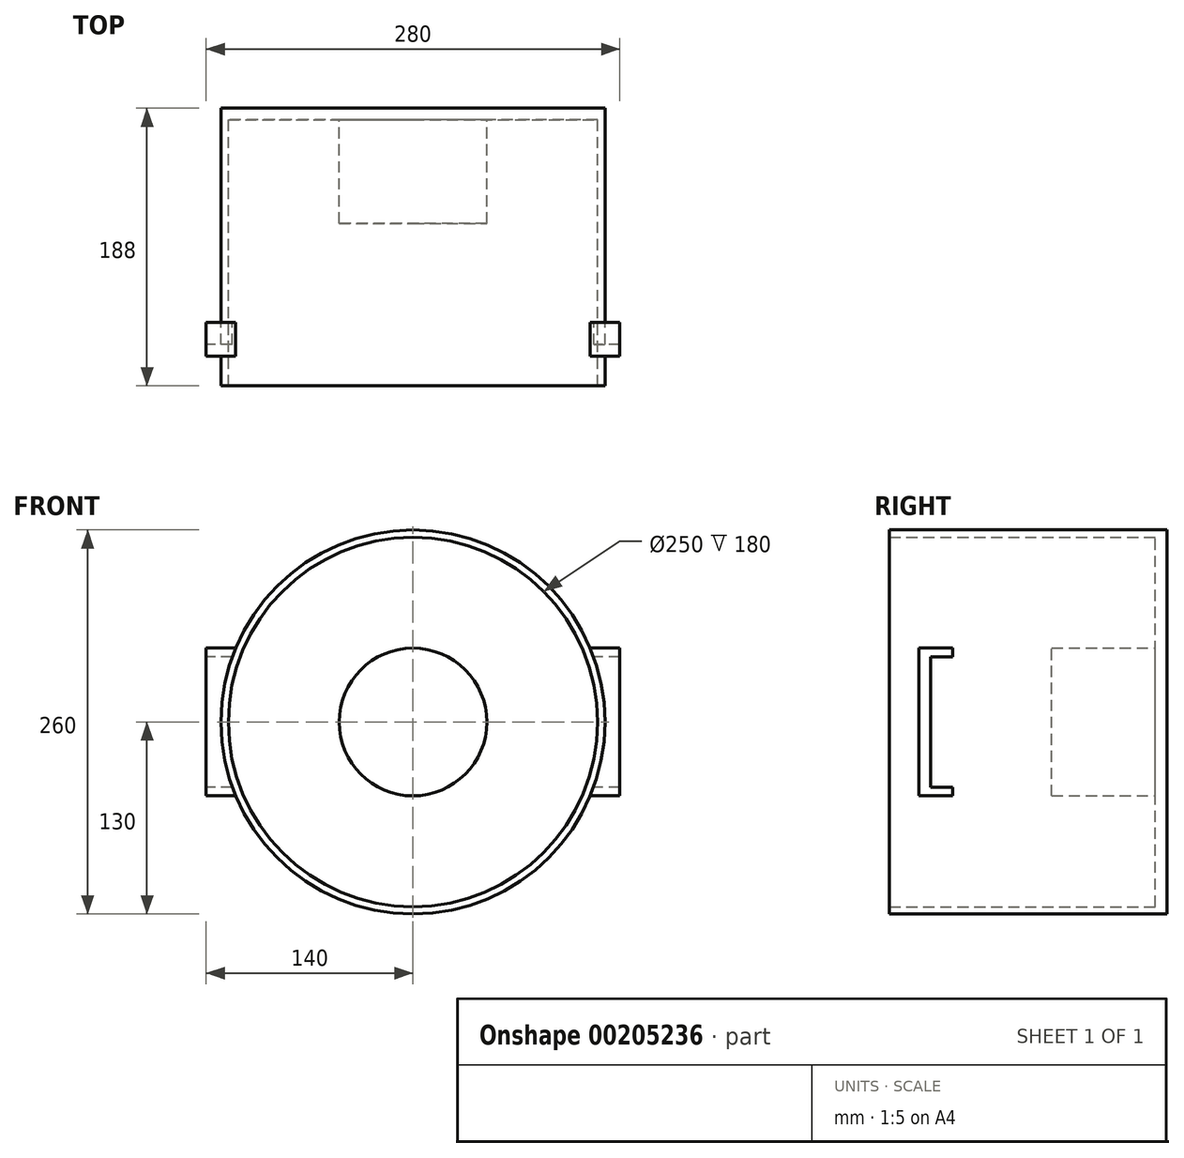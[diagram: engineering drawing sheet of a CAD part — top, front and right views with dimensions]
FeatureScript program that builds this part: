
annotation { "Feature Type Name" : "Feature", "Feature Type Description" : "" }
export const myFeature = defineFeature(function(context is Context, id is Id, definition is map)
    precondition{}
    {
        {
            var Q0;
            Q0=qCreatedBy(makeId("Front.planeOp"),FACE);
            var sketch = newSketch(context, id + "F0", { "sketchPlane" : qUnion([Q0])});
            skCircle(sketch, "E0", {"center": v(0, 0) * mm, "radius": 130 * mm});
            skSolve(sketch);
        }
        {
            var Q0;
            Q0 = qSketchRegion(id + "F0", true);
            extrude(context, id + "F1", {"entities" : qUnion([Q0]), "depth" : 8 * mm});
        }
        {
            var Q0;
            Q0=makeQuery(id+"F1.opExtrude","CAP_FACE",FACE,{"disambiguationData":[OSD([sQuery(id+"F0.wireOp",EDGE,"E0")])],"isStart":false});
            var sketch = newSketch(context, id + "F2", { "sketchPlane" : qUnion([Q0])});
            skCircle(sketch, "E1", {"center": v(0, 0) * mm, "radius": 130 * mm});
            skCircle(sketch, "E2", {"center": v(0, 0) * mm, "radius": 125 * mm});
            skSolve(sketch);
        }
        {
            var Q0;
            Q0=makeQuery(id+"F2.imprint","IMPRINT",FACE,{"disambiguationData":[TD([[makeQuery(id+"F2.imprint","IMPRINT",EDGE,{"derivedFrom":sQuery(id+"F2.wireOp",EDGE,"E1")}),1.0]])]});
            extrude(context, id + "F3", {"entities" : qUnion([Q0]), "operationType" : NewBodyOperationType.ADD, "depth" : 180 * mm});
        }
        {
            var Q0;
            Q0=makeQuery(id+"F1.opExtrude","CAP_FACE",FACE,{"disambiguationData":[OSD([sQuery(id+"F0.wireOp",EDGE,"E0")])],"isStart":false});
            var sketch = newSketch(context, id + "F4", { "sketchPlane" : qUnion([Q0])});
            skCircle(sketch, "E3", {"center": v(0, 0) * mm, "radius": 50 * mm});
            skSolve(sketch);
        }
        {
            var Q0;
            Q0=makeQuery(id+"F4.imprint","IMPRINT",FACE,{"disambiguationData":[TD([[makeQuery(id+"F4.imprint","IMPRINT",EDGE,{"derivedFrom":sQuery(id+"F4.wireOp",EDGE,"E3")}),1.0]])]});
            extrude(context, id + "F5", {"entities" : qUnion([Q0]), "operationType" : NewBodyOperationType.ADD, "depth" : 70 * mm});
        }
        {
            var Q0;
            Q0=qCreatedBy(makeId("Right.planeOp"),FACE);
            var sketch = newSketch(context, id + "F6", { "sketchPlane" : qUnion([Q0])});
            skLineSegment(sketch, "E4.bottom", {"start": v(-168, 50) * mm, "end": v(-160, 50) * mm});
            skLineSegment(sketch, "E4.top", {"start": v(-168, -50) * mm, "end": v(-160, -50) * mm});
            skLineSegment(sketch, "E4.left", {"start": v(-168, 50) * mm, "end": v(-168, -50) * mm});
            skLineSegment(sketch, "E4.right", {"start": v(-160, 50) * mm, "end": v(-160, -50) * mm});
            skPoint(sketch, "E4.middle", {"position": v(-164, 0) * mm});
            skLineSegment(sketch, "E5.bottom", {"start": v(-160, 50) * mm, "end": v(-145, 50) * mm});
            skLineSegment(sketch, "E5.top", {"start": v(-160, 44) * mm, "end": v(-145, 44) * mm});
            skLineSegment(sketch, "E5.left", {"start": v(-160, 50) * mm, "end": v(-160, 44) * mm});
            skLineSegment(sketch, "E5.right", {"start": v(-145, 50) * mm, "end": v(-145, 44) * mm});
            skLineSegment(sketch, "E6.MirrorCS", {"start": v(-145, -50) * mm, "end": v(-145, -44) * mm});
            skLineSegment(sketch, "E7.MirrorCS", {"start": v(-160, -44) * mm, "end": v(-145, -44) * mm});
            skLineSegment(sketch, "E8.MirrorCS", {"start": v(-160, -50) * mm, "end": v(-145, -50) * mm});
            skSolve(sketch);
        }
        {
            var Q0;
            Q0=makeQuery(id+"F6.imprint","IMPRINT",FACE,{"disambiguationData":[TD([[makeQuery(id+"F6.imprint","IMPRINT",EDGE,{"derivedFrom":sQuery(id+"F6.wireOp",EDGE,"E4.bottom")}),-1.0]])]});
            var Q1;
            Q1=makeQuery(id+"F6.imprint","IMPRINT",FACE,{"disambiguationData":[TD([[makeQuery(id+"F6.imprint","IMPRINT",EDGE,{"derivedFrom":sQuery(id+"F6.wireOp",EDGE,"E5.bottom")}),-1.0]])]});
            var Q2;
            Q2=makeQuery(id+"F6.imprint","IMPRINT",FACE,{"disambiguationData":[TD([[makeQuery(id+"F6.imprint","IMPRINT",EDGE,{"derivedFrom":sQuery(id+"F6.wireOp",EDGE,"E6.MirrorCS")}),1.0]])]});
            extrude(context, id + "F7", {"entities" : qUnion([Q0, Q1, Q2]), "operationType" : NewBodyOperationType.ADD, "endBound" : BoundingType.SYMMETRIC, "depth" : 280 * mm});
        }
        {
            var Q0;
            Q0=makeQuery(id+"F7.boolean.opBoolean","SPLIT",FACE,{"disambiguationData":[TD([makeQuery(id+"F3.opExtrude","SWEPT_FACE",FACE,{"disambiguationData":[OSD([sQuery(id+"F2.wireOp",EDGE,"E2")])]})])],"derivedFrom":makeQuery(id+"F7.opExtrude","SWEPT_FACE",FACE,{"disambiguationData":[OSD([sQuery(id+"F6.wireOp",EDGE,"E4.left")])]})});
            extrude(context, id + "F8", {"entities" : qUnion([Q0]), "operationType" : NewBodyOperationType.REMOVE, "oppositeDirection" : true, "depth" : 25 * mm});
        }
    });
